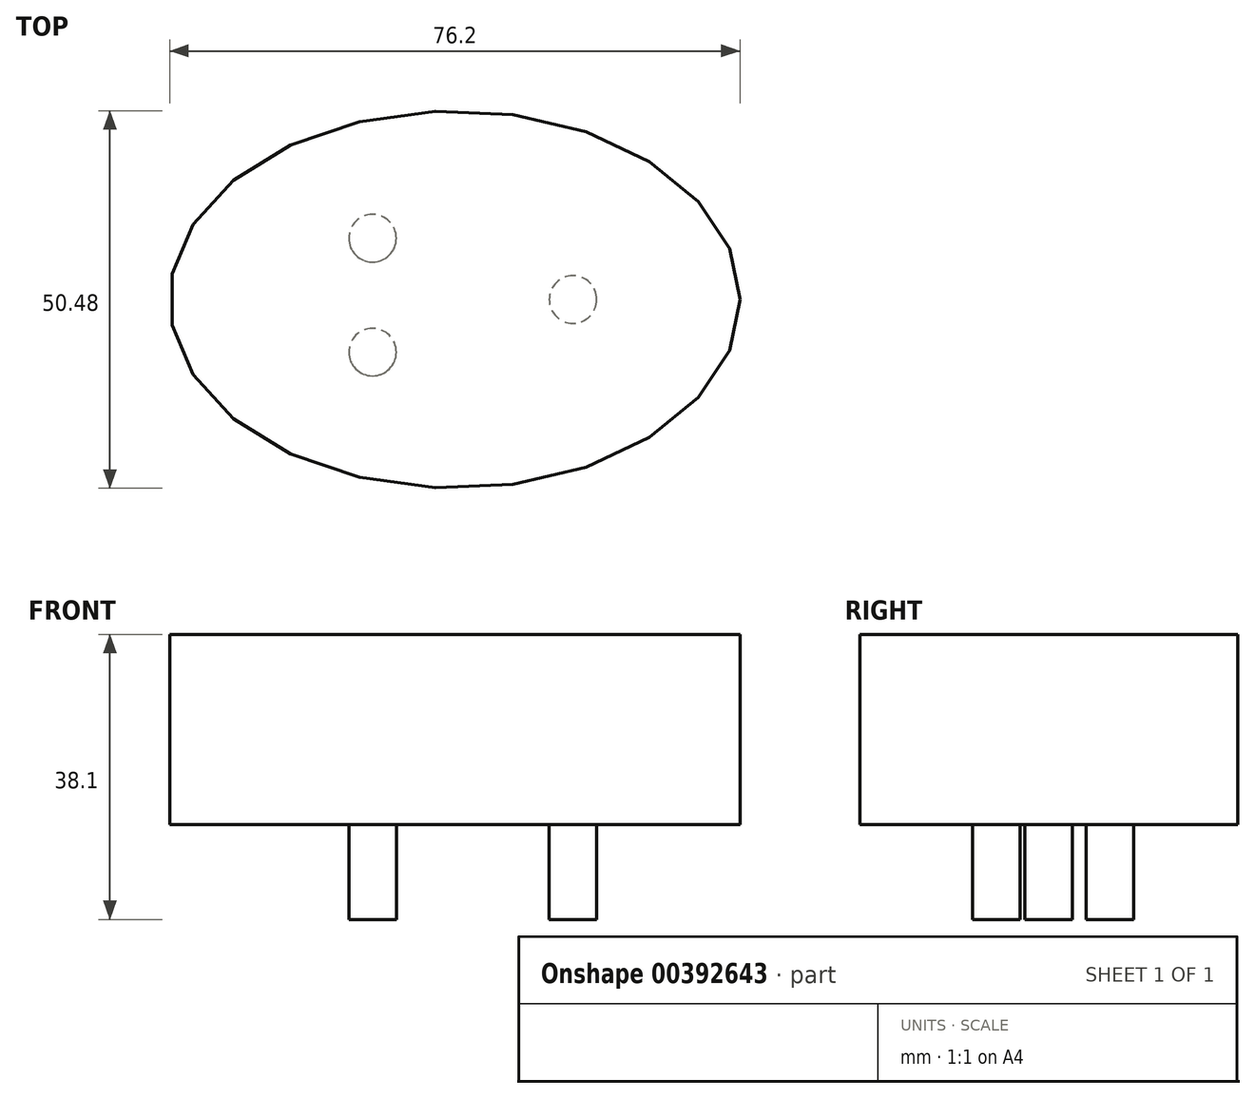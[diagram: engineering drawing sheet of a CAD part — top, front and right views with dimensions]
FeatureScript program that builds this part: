
annotation { "Feature Type Name" : "Feature", "Feature Type Description" : "" }
export const myFeature = defineFeature(function(context is Context, id is Id, definition is map)
    precondition{}
    {
        {
            var Q0;
            Q0=qCreatedBy(makeId("Top.planeOp"),FACE);
            var sketch = newSketch(context, id + "F0", { "sketchPlane" : qUnion([Q0])});
            skEllipse(sketch, "E0", {"center": v(0, 0) * mm, "majorRadius": 38.1 * mm, "minorRadius": 25.24 * mm, "majorAxis": v(1, 0)});
            skSolve(sketch);
        }
        {
            var Q0;
            Q0=makeQuery(id+"F0.imprint","IMPRINT",FACE,{"disambiguationData":[TD([[makeQuery(id+"F0.imprint","IMPRINT",EDGE,{"derivedFrom":sQuery(id+"F0.wireOp",EDGE,"E0")}),1.0]])]});
            extrude(context, id + "F1", {"entities" : qUnion([Q0]), "depth" : 25.4 * mm});
        }
        {
            var Q0;
            Q0=makeQuery(id+"F1.opExtrude","CAP_FACE",FACE,{"disambiguationData":[OSD([sQuery(id+"F0.wireOp",EDGE,"E0")])],"isStart":true});
            var sketch = newSketch(context, id + "F2", { "sketchPlane" : qUnion([Q0])});
            skCircle(sketch, "E1", {"center": v(15.79, 0) * mm, "radius": 3.18 * mm});
            skCircle(sketch, "E2", {"center": v(-11, -8.18) * mm, "radius": 3.18 * mm});
            skCircle(sketch, "E3", {"center": v(-11, 7.03) * mm, "radius": 3.18 * mm});
            skSolve(sketch);
        }
        {
            var Q0;
            Q0=makeQuery(id+"F2.imprint","IMPRINT",FACE,{"disambiguationData":[TD([[makeQuery(id+"F2.imprint","IMPRINT",EDGE,{"derivedFrom":sQuery(id+"F2.wireOp",EDGE,"E1")}),1.0]])]});
            extrude(context, id + "F3", {"entities" : qUnion([Q0]), "operationType" : NewBodyOperationType.ADD, "depth" : 12.7 * mm});
        }
        {
            var Q0;
            Q0=makeQuery(id+"F2.imprint","IMPRINT",FACE,{"disambiguationData":[TD([[makeQuery(id+"F2.imprint","IMPRINT",EDGE,{"derivedFrom":sQuery(id+"F2.wireOp",EDGE,"E3")}),1.0]])]});
            var Q1;
            Q1=makeQuery(id+"F2.imprint","IMPRINT",FACE,{"disambiguationData":[TD([[makeQuery(id+"F2.imprint","IMPRINT",EDGE,{"derivedFrom":sQuery(id+"F2.wireOp",EDGE,"E2")}),1.0]])]});
            extrude(context, id + "F4", {"entities" : qUnion([Q0, Q1]), "operationType" : NewBodyOperationType.ADD, "depth" : 12.7 * mm});
        }
    });
